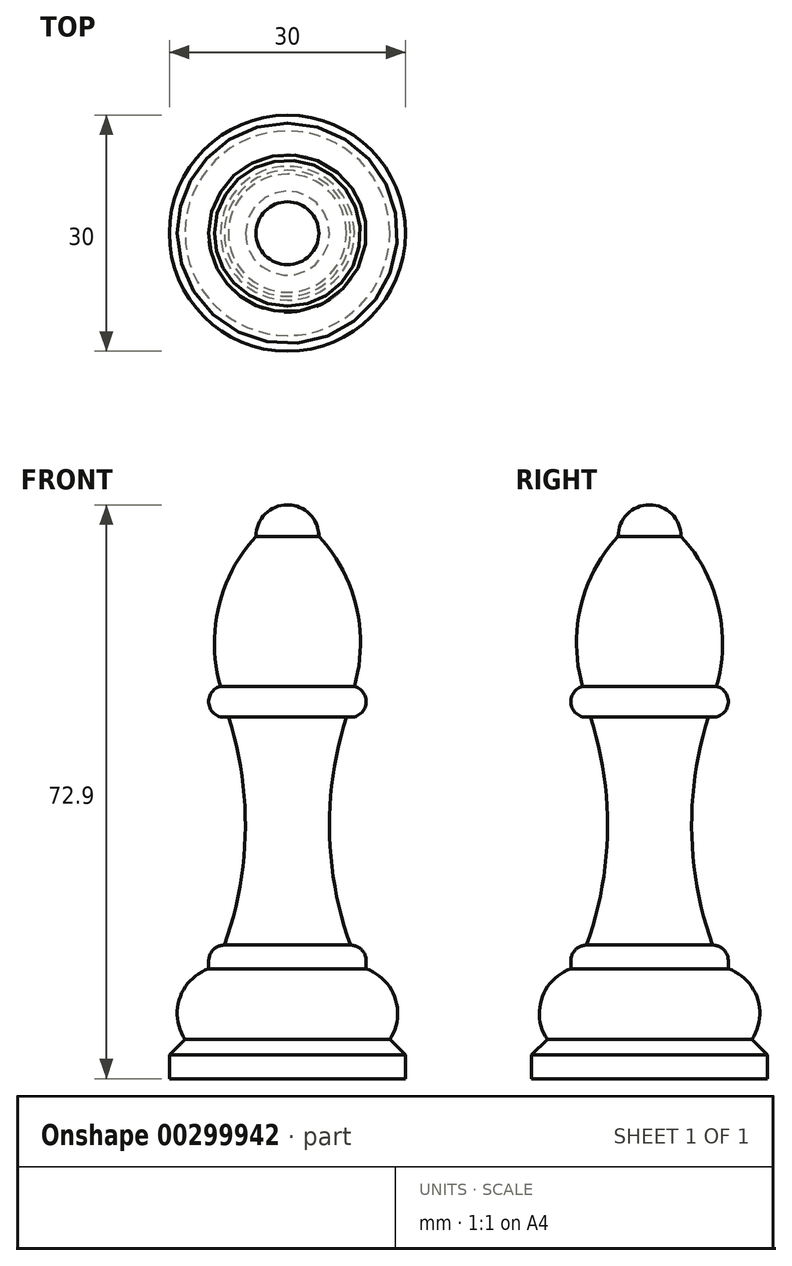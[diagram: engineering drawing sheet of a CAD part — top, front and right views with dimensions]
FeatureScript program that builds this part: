
annotation { "Feature Type Name" : "Feature", "Feature Type Description" : "" }
export const myFeature = defineFeature(function(context is Context, id is Id, definition is map)
    precondition{}
    {
        {
            var Q0;
            Q0=qCreatedBy(makeId("Front.planeOp"),FACE);
            var sketch = newSketch(context, id + "F0", { "sketchPlane" : qUnion([Q0])});
            skArc(sketch, "E0", {"start": v(4, -4) * mm, "mid": v(2.83, -1.17) * mm, "end": v(0, 0) * mm});
            skArc(sketch, "E1", {"start": v(8.5, -23.06) * mm, "mid": v(8.74, -12.94) * mm, "end": v(4, -4) * mm});
            skArc(sketch, "E2", {"start": v(8.5, -26.93) * mm, "mid": v(10, -25) * mm, "end": v(8.5, -23.06) * mm});
            skLineSegment(sketch, "E3", {"start": v(8.5, -26.93) * mm, "end": v(7.5, -26.93) * mm});
            skArc(sketch, "E4", {"start": v(7.5, -26.93) * mm, "mid": v(5.35, -41.47) * mm, "end": v(8, -55.93) * mm});
            skArc(sketch, "E5", {"start": v(10, -57.93) * mm, "mid": v(9.41, -56.52) * mm, "end": v(8, -55.93) * mm});
            skLineSegment(sketch, "E6", {"start": v(10, -57.93) * mm, "end": v(10, -58.93) * mm});
            skLineSegment(sketch, "E7", {"start": v(13, -67.9) * mm, "end": v(15, -69.9) * mm});
            skLineSegment(sketch, "E8", {"start": v(15, -69.9) * mm, "end": v(15, -72.9) * mm});
            skLineSegment(sketch, "E9", {"start": v(15, -72.9) * mm, "end": v(0, -72.9) * mm});
            skLineSegment(sketch, "E10", {"start": v(0, -72.9) * mm, "end": v(0, 0) * mm});
            skArc(sketch, "E11", {"start": v(13, -67.9) * mm, "mid": v(13.69, -62.69) * mm, "end": v(10, -58.93) * mm});
            skSolve(sketch);
        }
        {
            var Q0;
            Q0=makeQuery(id+"F0.imprint","IMPRINT",FACE,{"disambiguationData":[TD([[makeQuery(id+"F0.imprint","IMPRINT",EDGE,{"derivedFrom":sQuery(id+"F0.wireOp",EDGE,"E0")}),1.0]])]});
            var Q1;
            Q1=sQuery(id+"F0.wireOp",EDGE,"E10");
            revolve(context, id + "F1", {"entities" : qUnion([Q0]), "axis" : qUnion([Q1]), "revolveType" : RevolveType.FULL});
        }
    });
